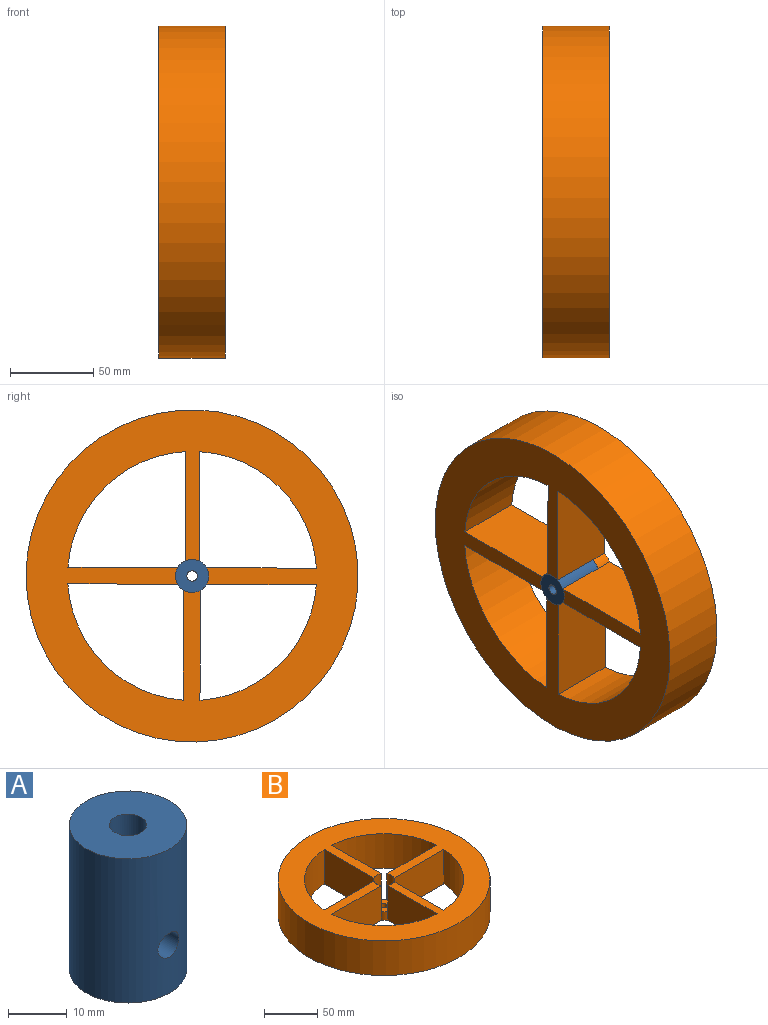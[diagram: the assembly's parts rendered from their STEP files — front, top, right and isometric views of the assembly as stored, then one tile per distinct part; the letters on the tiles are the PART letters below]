
ASSEMBLY  parts=2 mates=1
PART A: 6 faces, bbox 20x20x30 mm
  f0: cylinder r=3.17mm len=30mm, axis (0,0,-1), area 554.1mm2, adj f2,f3,f4,f5
  f1: cylinder r=10mm len=30mm, axis (0,0,-1), area 1845.4mm2, adj f2,f3,f4,f5
  f2: plane 20x20mm, normal (0,0,1), area 282.6mm2, adj f0,f1
  f3: plane 20x20mm, normal (0,0,-1), area 282.6mm2, adj f0,f1
  f4: cylinder r=2.5mm len=8.05mm, axis (0,-1,0), area 113.8mm2, adj f0,f1
  f5: cylinder r=2.5mm len=8.05mm, axis (0,-1,0), area 113.8mm2, adj f0,f1
PART B: 25 faces, bbox 200x200x40 mm
  f0: cylinder r=75mm len=70.67mm, axis (0,0,-1), area 4345.5mm2, adj f1,f16,f17,f18
  f1: plane 65.79x40mm, normal (1,0,0), area 2631.7mm2, adj f0,f2,f17,f18,f19
  f2: cylinder r=10mm len=30mm, axis (0,0,-1), area 257.9mm2, adj f1,f3,f17,f24
  f3: plane 65.79x40mm, normal (-1,0,0), area 2631.7mm2, adj f2,f4,f17,f18,f20
  f4: cylinder r=75mm len=70.67mm, axis (0,0,-1), area 4345.5mm2, adj f3,f5,f17,f18
  f5: plane 66.17x40mm, normal (0,-1,0), area 2646.9mm2, adj f4,f6,f17,f18,f20
  f6: cylinder r=10mm len=30mm, axis (0,0,-1), area 314.2mm2, adj f5,f7,f17,f24
  f7: plane 66.17x40mm, normal (0,1,0), area 2646.9mm2, adj f6,f8,f17,f18,f21
  f8: cylinder r=75mm len=69.83mm, axis (0,0,-1), area 4312.1mm2, adj f7,f9,f17,f18
  f9: plane 66.17x40mm, normal (-1,0,0), area 2646.9mm2, adj f8,f10,f17,f18,f21
  f10: cylinder r=10mm len=30mm, axis (0,0,-1), area 314.2mm2, adj f9,f11,f17,f24
  f11: plane 66.17x40mm, normal (1,0,0), area 2646.9mm2, adj f10,f12,f17,f18,f22
  f12: cylinder r=75mm len=69.83mm, axis (0,0,-1), area 4312.1mm2, adj f11,f13,f17,f18
  f13: plane 66.17x40mm, normal (0,1,0), area 2646.9mm2, adj f12,f14,f17,f18,f22
  f14: cylinder r=10mm len=30mm, axis (0,0,-1), area 314.2mm2, adj f13,f16,f17,f24
  f15: cylinder r=100mm len=200mm, axis (0,0,-1), area 25132.7mm2, adj f17,f18
  f16: plane 66.17x40mm, normal (0,-1,0), area 2646.9mm2, adj f0,f14,f17,f18,f19
  f17: plane 200x200mm, normal (0,0,1), area 16249.6mm2, adj f0,f1,f2,f3,f4,f5,f6,f7
  f18: plane 200x200mm, normal (0,0,-1), area 16532.2mm2, adj f0,f1,f3,f4,f5,f7,f8,f9
  f19: cylinder r=10mm len=10mm, axis (0,0,-1), area 61.7mm2, adj f1,f16,f18,f24
  f20: cylinder r=10mm len=10mm, axis (0,0,-1), area 61.7mm2, adj f3,f5,f18,f24
  f21: cylinder r=10mm len=10mm, axis (0,0,-1), area 52.4mm2, adj f7,f9,f18,f24
  f22: cylinder r=10mm len=10mm, axis (0,0,-1), area 52.4mm2, adj f11,f13,f18,f24
  f23: cylinder r=3.17mm len=10mm, axis (0,0,-1), area 199.2mm2, adj f18,f24
  f24: plane 20x20mm, normal (0,0,1), area 282.6mm2, adj f2,f6,f10,f14,f19,f20,f21,f22
PLACE A rot(axis=(-0.58,-0.58,0.58),120deg) t=(15,0,10)mm
PLACE B rot(axis=(-0.58,-0.58,0.58),119.9deg) t=(25,0,0)mm
MATE revolute A.f0 <-> B.f23  axis (1,0,0) through (15,0,0)mm
